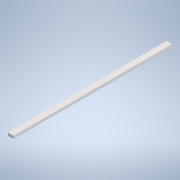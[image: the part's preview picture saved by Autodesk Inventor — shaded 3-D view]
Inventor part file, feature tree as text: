
AUTODESK INVENTOR PART (.ipt)
format: ipt  version: 2021.2 (Build 252289000, 289)  size: 108,032 bytes
history: native  units: in
note: dims shown in document units (in); Inventor stores cm internally (conversion verified against a paired STEP export)
features: move_body x2, direct_edit x1, extrude x1, other x1
ambient origin geometry x8: Origin, YZ Plane, XZ Plane, XY Plane, X Axis, Y Axis, Z Axis, Center Point
bodies: Solid1 (feature_tree)
feature tree (5):
  direct_edit  "Direct Edit1"
  extrude  "Extrude1"  Depth=5.0in TaperAngle=0.0deg
  move_body  "Move1"
  move_body  "Move2"
  other  "Size1"
